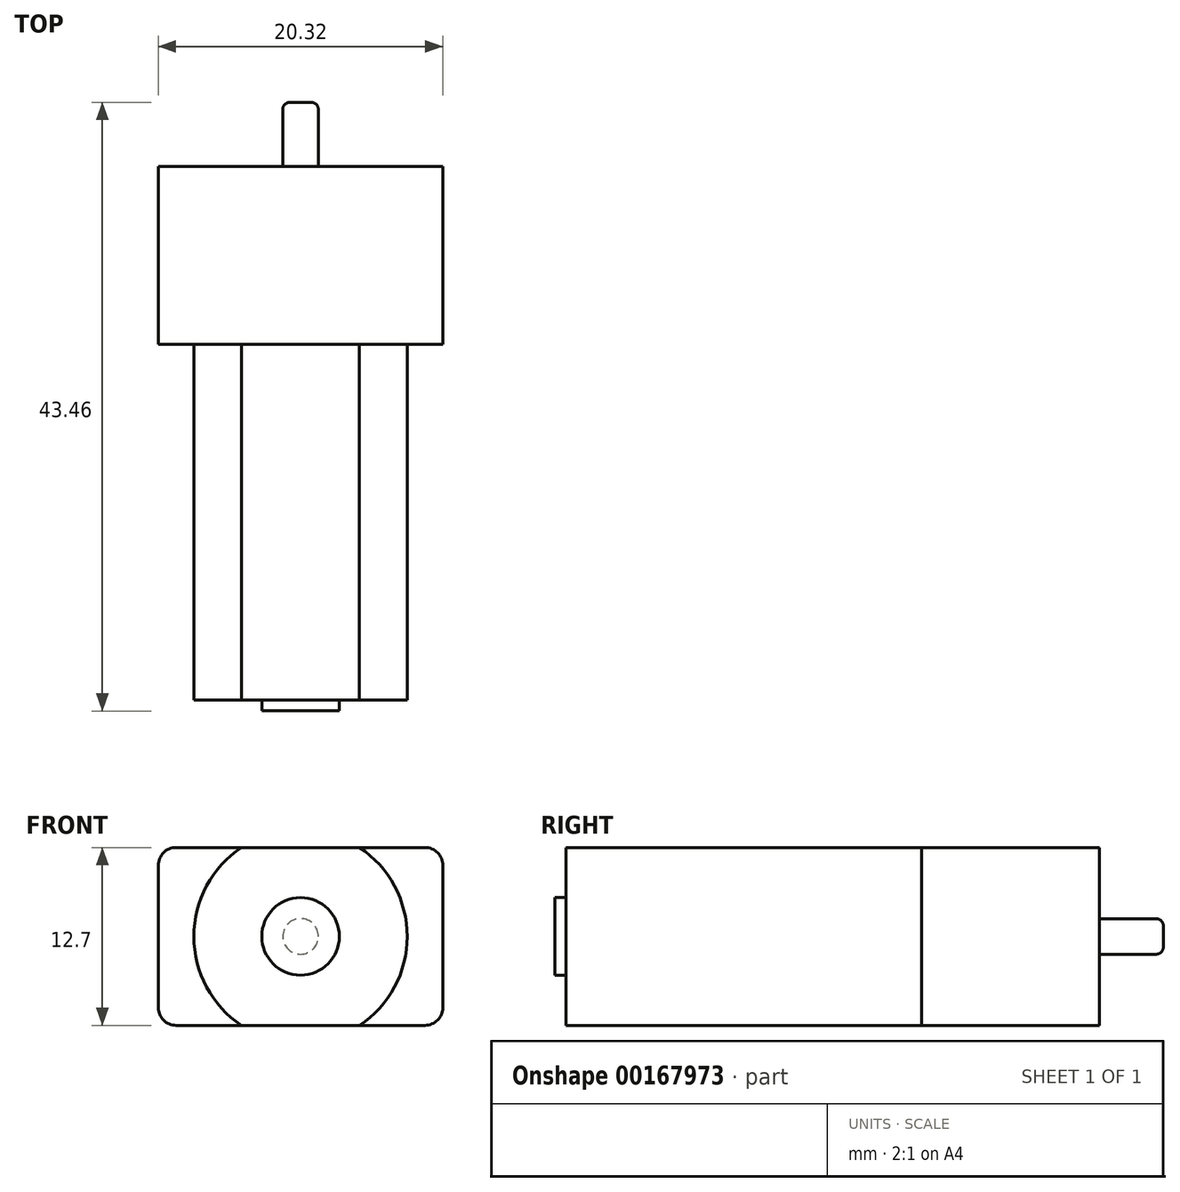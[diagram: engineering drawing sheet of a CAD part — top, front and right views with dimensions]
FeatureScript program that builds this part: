
annotation { "Feature Type Name" : "Feature", "Feature Type Description" : "" }
export const myFeature = defineFeature(function(context is Context, id is Id, definition is map)
    precondition{}
    {
        {
            var Q0;
            Q0=qCreatedBy(makeId("Front.planeOp"),FACE);
            var sketch = newSketch(context, id + "F0", { "sketchPlane" : qUnion([Q0])});
            skCircle(sketch, "E0", {"center": v(0, 0) * mm, "radius": 2.77 * mm});
            skArc(sketch, "E1", {"start": v(-4.21, 6.35) * mm, "mid": v(-7.62, 0) * mm, "end": v(-4.21, -6.35) * mm});
            skLineSegment(sketch, "E2.bottom", {"start": v(-4.21, 6.35) * mm, "end": v(4.21, 6.35) * mm});
            skLineSegment(sketch, "E2.top", {"start": v(-4.21, -6.35) * mm, "end": v(4.21, -6.35) * mm});
            skArc(sketch, "E3.trimOffspring", {"start": v(4.21, -6.35) * mm, "mid": v(7.62, 0) * mm, "end": v(4.21, 6.35) * mm});
            skSolve(sketch);
        }
        {
            var Q0;
            Q0=makeQuery(id+"F0.imprint","IMPRINT",FACE,{"disambiguationData":[TD([[makeQuery(id+"F0.imprint","IMPRINT",EDGE,{"derivedFrom":sQuery(id+"F0.wireOp",EDGE,"E0")}),1.0]])]});
            var Q1;
            Q1=makeQuery(id+"F0.imprint","IMPRINT",FACE,{"disambiguationData":[TD([[makeQuery(id+"F0.imprint","IMPRINT",EDGE,{"derivedFrom":sQuery(id+"F0.wireOp",EDGE,"E0")}),-1.0]])]});
            extrude(context, id + "F1", {"entities" : qUnion([Q0, Q1]), "oppositeDirection" : true, "depth" : 25.4 * mm});
        }
        {
            var Q0;
            Q0=makeQuery(id+"F0.imprint","IMPRINT",FACE,{"disambiguationData":[TD([[makeQuery(id+"F0.imprint","IMPRINT",EDGE,{"derivedFrom":sQuery(id+"F0.wireOp",EDGE,"E0")}),1.0]])]});
            extrude(context, id + "F2", {"entities" : qUnion([Q0]), "operationType" : NewBodyOperationType.ADD, "depth" : 0.79 * mm});
        }
        {
            var Q0;
            Q0=makeQuery(id+"F1.opExtrude","CAP_FACE",FACE,{"disambiguationData":[OSD([sQuery(id+"F0.wireOp",EDGE,"E1"),sQuery(id+"F0.wireOp",EDGE,"E2.bottom"),sQuery(id+"F0.wireOp",EDGE,"E2.top"),sQuery(id+"F0.wireOp",EDGE,"E3.trimOffspring")])],"isStart":false});
            var sketch = newSketch(context, id + "F3", { "sketchPlane" : qUnion([Q0])});
            skLineSegment(sketch, "E4.0", {"start": v(4.21, 6.35) * mm, "end": v(-4.21, 6.35) * mm});
            skLineSegment(sketch, "E4.1", {"start": v(4.21, -6.35) * mm, "end": v(-4.21, -6.35) * mm});
            skLineSegment(sketch, "E5.bottom", {"start": v(-8.9, 6.35) * mm, "end": v(8.9, 6.35) * mm});
            skLineSegment(sketch, "E5.top", {"start": v(-8.9, -6.35) * mm, "end": v(8.9, -6.35) * mm});
            skLineSegment(sketch, "E5.left", {"start": v(-10.16, 5.08) * mm, "end": v(-10.16, -5.08) * mm});
            skLineSegment(sketch, "E5.right", {"start": v(10.16, 5.08) * mm, "end": v(10.16, -5.08) * mm});
            skPoint(sketch, "E5.middle", {"position": v(0, 0) * mm});
            skPoint(sketch, "E6.visualSharp", {"position": v(-10.16, 6.35) * mm});
            skArc(sketch, "E6.filletArc", {"start": v(-8.9, 6.35) * mm, "mid": v(-9.79, 5.98) * mm, "end": v(-10.16, 5.08) * mm});
            skPoint(sketch, "E7.visualSharp", {"position": v(10.16, 6.35) * mm});
            skArc(sketch, "E7.filletArc", {"start": v(10.16, 5.08) * mm, "mid": v(9.79, 5.98) * mm, "end": v(8.9, 6.35) * mm});
            skPoint(sketch, "E8.visualSharp", {"position": v(10.16, -6.35) * mm});
            skArc(sketch, "E8.filletArc", {"start": v(8.9, -6.35) * mm, "mid": v(9.79, -5.98) * mm, "end": v(10.16, -5.08) * mm});
            skPoint(sketch, "E9.visualSharp", {"position": v(-10.16, -6.35) * mm});
            skArc(sketch, "E9.filletArc", {"start": v(-10.16, -5.08) * mm, "mid": v(-9.79, -5.98) * mm, "end": v(-8.9, -6.35) * mm});
            skSolve(sketch);
        }
        {
            var Q0;
            Q0=makeQuery(id+"F3.imprint","IMPRINT",FACE,{"disambiguationData":[TD([[makeQuery(id+"F3.imprint","IMPRINT",EDGE,{"derivedFrom":sQuery(id+"F3.wireOp",EDGE,"E5.right")}),-1.0]])]});
            var Q1;
            {var subQ1=makeQuery(id+"F1.opExtrude","CAP_EDGE",EDGE,{"disambiguationData":[OSD([sQuery(id+"F0.wireOp",EDGE,"E1")])],"isStart":false});Q1=makeQuery(id+"F3.imprint","IMPRINT",FACE,{"disambiguationData":[TD([[makeQuery(id+"F3.imprint","IMPRINT",EDGE,{"derivedFrom":subQ1}),-1.0]])]});}
            var Q2;
            Q2=makeQuery(id+"F3.imprint","IMPRINT",FACE,{"disambiguationData":[TD([[makeQuery(id+"F3.imprint","IMPRINT",EDGE,{"derivedFrom":sQuery(id+"F3.wireOp",EDGE,"E5.left")}),1.0]])]});
            extrude(context, id + "F4", {"entities" : qUnion([Q0, Q1, Q2]), "depth" : 12.7 * mm});
        }
        {
            var Q0;
            Q0=makeQuery(id+"F4.opExtrude","CAP_FACE",FACE,{"disambiguationData":[OSD([sQuery(id+"F3.wireOp",EDGE,"E5.bottom"),sQuery(id+"F3.wireOp",EDGE,"E5.top"),sQuery(id+"F3.wireOp",EDGE,"E5.left"),sQuery(id+"F3.wireOp",EDGE,"E5.right"),sQuery(id+"F3.wireOp",EDGE,"E6.filletArc"),sQuery(id+"F3.wireOp",EDGE,"E7.filletArc"),sQuery(id+"F3.wireOp",EDGE,"E8.filletArc"),sQuery(id+"F3.wireOp",EDGE,"E9.filletArc")])],"isStart":false});
            var sketch = newSketch(context, id + "F5", { "sketchPlane" : qUnion([Q0])});
            skCircle(sketch, "E10", {"center": v(0, 0) * mm, "radius": 1.27 * mm});
            skSolve(sketch);
        }
        {
            var Q0;
            Q0=makeQuery(id+"F5.imprint","IMPRINT",FACE,{"disambiguationData":[TD([[makeQuery(id+"F5.imprint","IMPRINT",EDGE,{"derivedFrom":sQuery(id+"F5.wireOp",EDGE,"E10")}),1.0]])]});
            extrude(context, id + "F6", {"entities" : qUnion([Q0]), "operationType" : NewBodyOperationType.ADD, "depth" : 4.57 * mm});
        }
        {
            var Q0;
            Q0=makeQuery(id+"F6.opExtrude","CAP_EDGE",EDGE,{"disambiguationData":[OSD([sQuery(id+"F5.wireOp",EDGE,"E10")])],"isStart":false});
            fillet(context, id + "F7", {"entities" : qUnion([Q0]), "radius" : 0.5 * mm, "tangentPropagation" : true, "allowEdgeOverflow" : false});
        }
    });
